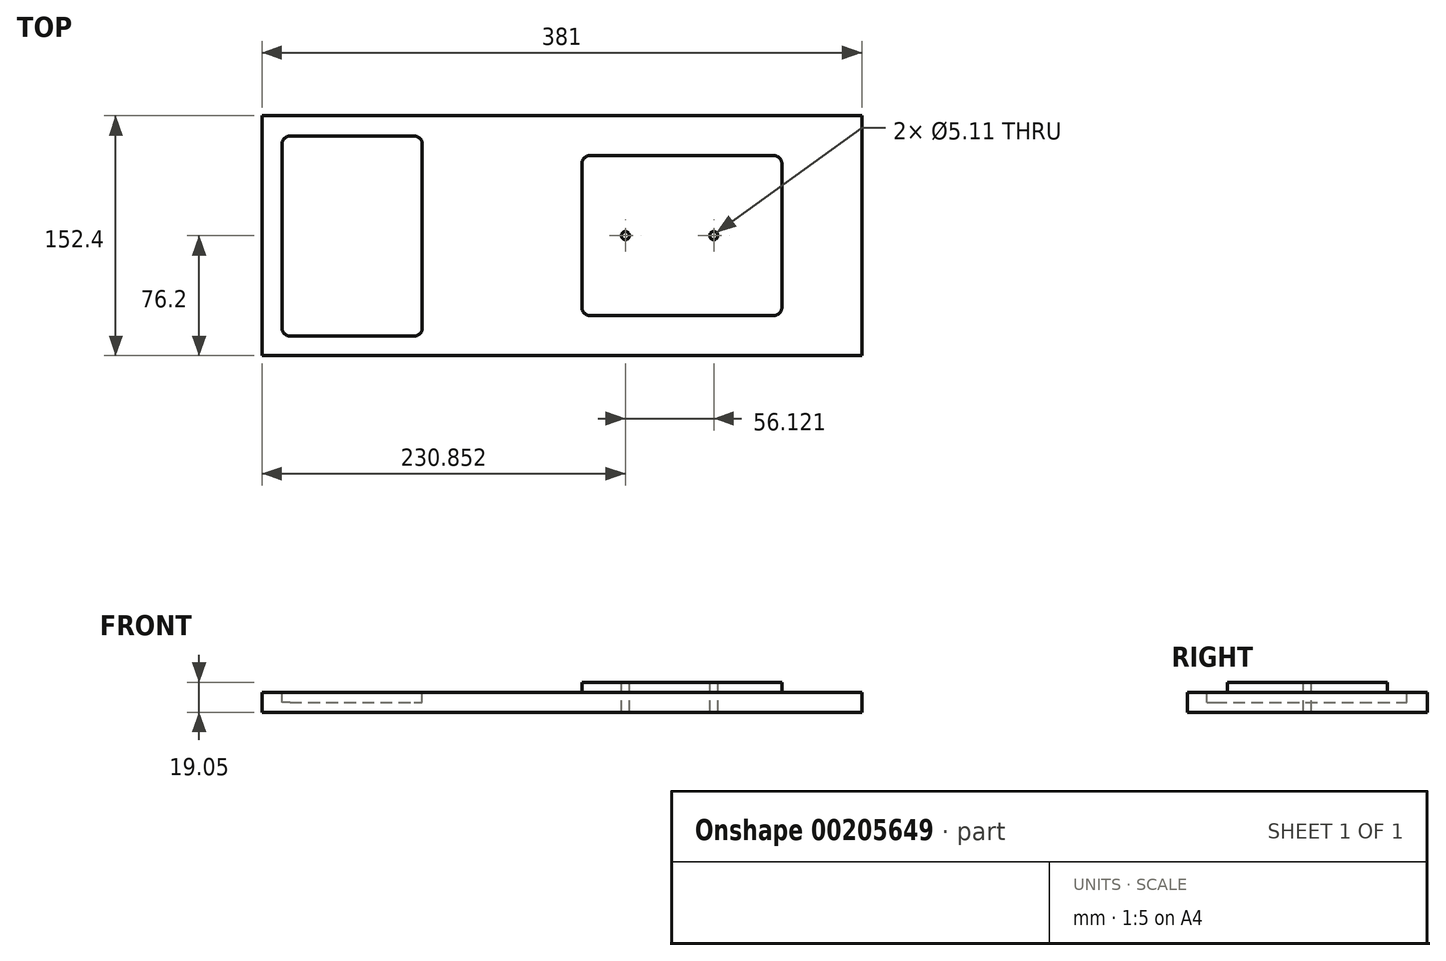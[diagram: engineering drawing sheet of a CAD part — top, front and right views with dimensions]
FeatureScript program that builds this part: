
annotation { "Feature Type Name" : "Feature", "Feature Type Description" : "" }
export const myFeature = defineFeature(function(context is Context, id is Id, definition is map)
    precondition{}
    {
        {
            var Q0;
            Q0=qCreatedBy(makeId("Top.planeOp"),FACE);
            var sketch = newSketch(context, id + "F0", { "sketchPlane" : qUnion([Q0])});
            skLineSegment(sketch, "E0.bottom", {"start": v(190.5, 76.2) * mm, "end": v(-190.5, 76.2) * mm});
            skLineSegment(sketch, "E0.top", {"start": v(190.5, -76.2) * mm, "end": v(-190.5, -76.2) * mm});
            skLineSegment(sketch, "E0.left", {"start": v(190.5, 76.2) * mm, "end": v(190.5, -76.2) * mm});
            skLineSegment(sketch, "E0.right", {"start": v(-190.5, 76.2) * mm, "end": v(-190.5, -76.2) * mm});
            skPoint(sketch, "E0.middle", {"position": v(0, 0) * mm});
            skSolve(sketch);
        }
        {
            var Q0;
            Q0=makeQuery(id+"F0.imprint","IMPRINT",FACE,{"disambiguationData":[TD([[makeQuery(id+"F0.imprint","IMPRINT",EDGE,{"derivedFrom":sQuery(id+"F0.wireOp",EDGE,"E0.bottom")}),1.0]])]});
            extrude(context, id + "F1", {"entities" : qUnion([Q0]), "depth" : 12.7 * mm});
        }
        {
            var Q0;
            Q0=makeQuery(id+"F1.opExtrude","CAP_FACE",FACE,{"disambiguationData":[OSD([sQuery(id+"F0.wireOp",EDGE,"E0.bottom"),sQuery(id+"F0.wireOp",EDGE,"E0.top"),sQuery(id+"F0.wireOp",EDGE,"E0.left"),sQuery(id+"F0.wireOp",EDGE,"E0.right")])],"isStart":false});
            var sketch = newSketch(context, id + "F2", { "sketchPlane" : qUnion([Q0])});
            skLineSegment(sketch, "E1.bottom", {"start": v(-177.8, -63.74) * mm, "end": v(-88.66, -63.74) * mm});
            skLineSegment(sketch, "E1.top", {"start": v(-177.8, 63.26) * mm, "end": v(-88.66, 63.26) * mm});
            skLineSegment(sketch, "E1.left", {"start": v(-177.8, -63.74) * mm, "end": v(-177.8, 63.26) * mm});
            skLineSegment(sketch, "E1.right", {"start": v(-88.66, -63.74) * mm, "end": v(-88.66, 63.26) * mm});
            skSolve(sketch);
        }
        {
            var Q0;
            Q0=makeQuery(id+"F2.imprint","IMPRINT",FACE,{"disambiguationData":[TD([[makeQuery(id+"F2.imprint","IMPRINT",EDGE,{"derivedFrom":sQuery(id+"F2.wireOp",EDGE,"E1.bottom")}),1.0]])]});
            extrude(context, id + "F3", {"entities" : qUnion([Q0]), "operationType" : NewBodyOperationType.REMOVE, "oppositeDirection" : true, "depth" : 6.35 * mm});
        }
        {
            var Q0;
            Q0=makeQuery(id+"F3.boolean.opBoolean","COPY",EDGE,{"derivedFrom":makeQuery(id+"F3.opExtrude","SWEPT_EDGE",EDGE,{"disambiguationData":[OSD([sQuery(id+"F2.wireOp",EDGE,"E1.top"),sQuery(id+"F2.wireOp",EDGE,"E1.left")])]})});
            var Q1;
            Q1=makeQuery(id+"F3.boolean.opBoolean","COPY",EDGE,{"derivedFrom":makeQuery(id+"F3.opExtrude","SWEPT_EDGE",EDGE,{"disambiguationData":[OSD([sQuery(id+"F2.wireOp",EDGE,"E1.bottom"),sQuery(id+"F2.wireOp",EDGE,"E1.left")])]})});
            var Q2;
            Q2=makeQuery(id+"F3.boolean.opBoolean","COPY",EDGE,{"derivedFrom":makeQuery(id+"F3.opExtrude","SWEPT_EDGE",EDGE,{"disambiguationData":[OSD([sQuery(id+"F2.wireOp",EDGE,"E1.top"),sQuery(id+"F2.wireOp",EDGE,"E1.right")])]})});
            var Q3;
            Q3=makeQuery(id+"F3.boolean.opBoolean","COPY",EDGE,{"derivedFrom":makeQuery(id+"F3.opExtrude","SWEPT_EDGE",EDGE,{"disambiguationData":[OSD([sQuery(id+"F2.wireOp",EDGE,"E1.bottom"),sQuery(id+"F2.wireOp",EDGE,"E1.right")])]})});
            fillet(context, id + "F4", {"entities" : qUnion([Q0, Q1, Q2, Q3]), "radius" : 5.08 * mm, "tangentPropagation" : true, "allowEdgeOverflow" : false});
        }
        {
            var Q0;
            Q0=makeQuery(id+"F1.opExtrude","CAP_FACE",FACE,{"disambiguationData":[OSD([sQuery(id+"F0.wireOp",EDGE,"E0.bottom"),sQuery(id+"F0.wireOp",EDGE,"E0.top"),sQuery(id+"F0.wireOp",EDGE,"E0.left"),sQuery(id+"F0.wireOp",EDGE,"E0.right")])],"isStart":false});
            var sketch = newSketch(context, id + "F5", { "sketchPlane" : qUnion([Q0])});
            skLineSegment(sketch, "E2", {"start": v(0, 0) * mm, "end": v(172.49, 0) * mm, "construction": true});
            skLineSegment(sketch, "E3.bottom", {"start": v(12.7, 50.8) * mm, "end": v(139.7, 50.8) * mm});
            skLineSegment(sketch, "E3.top", {"start": v(12.7, -50.8) * mm, "end": v(139.7, -50.8) * mm});
            skLineSegment(sketch, "E3.left", {"start": v(12.7, 50.8) * mm, "end": v(12.7, -50.8) * mm});
            skLineSegment(sketch, "E3.right", {"start": v(139.7, 50.8) * mm, "end": v(139.7, -50.8) * mm});
            skPoint(sketch, "E3.middle", {"position": v(76.2, 0) * mm});
            skSolve(sketch);
        }
        {
            var Q0;
            Q0=makeQuery(id+"F5.imprint","IMPRINT",FACE,{"disambiguationData":[TD([[makeQuery(id+"F5.imprint","IMPRINT",EDGE,{"derivedFrom":sQuery(id+"F5.wireOp",EDGE,"E3.bottom")}),-1.0]])]});
            extrude(context, id + "F6", {"entities" : qUnion([Q0]), "operationType" : NewBodyOperationType.ADD, "depth" : 6.35 * mm});
        }
        {
            var Q0;
            Q0=makeQuery(id+"F6.opExtrude","SWEPT_EDGE",EDGE,{"disambiguationData":[OSD([sQuery(id+"F5.wireOp",EDGE,"E3.top"),sQuery(id+"F5.wireOp",EDGE,"E3.left")])]});
            var Q1;
            Q1=makeQuery(id+"F6.opExtrude","SWEPT_EDGE",EDGE,{"disambiguationData":[OSD([sQuery(id+"F5.wireOp",EDGE,"E3.top"),sQuery(id+"F5.wireOp",EDGE,"E3.right")])]});
            var Q2;
            Q2=makeQuery(id+"F6.opExtrude","SWEPT_EDGE",EDGE,{"disambiguationData":[OSD([sQuery(id+"F5.wireOp",EDGE,"E3.bottom"),sQuery(id+"F5.wireOp",EDGE,"E3.right")])]});
            var Q3;
            Q3=makeQuery(id+"F6.opExtrude","SWEPT_EDGE",EDGE,{"disambiguationData":[OSD([sQuery(id+"F5.wireOp",EDGE,"E3.bottom"),sQuery(id+"F5.wireOp",EDGE,"E3.left")])]});
            fillet(context, id + "F7", {"entities" : qUnion([Q0, Q1, Q2, Q3]), "radius" : 5.08 * mm, "tangentPropagation" : true, "allowEdgeOverflow" : false});
        }
        {
            var Q0;
            Q0=makeQuery(id+"F6.opExtrude","CAP_FACE",FACE,{"disambiguationData":[OSD([sQuery(id+"F5.wireOp",EDGE,"E3.bottom"),sQuery(id+"F5.wireOp",EDGE,"E3.top"),sQuery(id+"F5.wireOp",EDGE,"E3.left"),sQuery(id+"F5.wireOp",EDGE,"E3.right")])],"isStart":false});
            var sketch = newSketch(context, id + "F8", { "sketchPlane" : qUnion([Q0])});
            skPoint(sketch, "E4", {"position": v(40.35, 0) * mm});
            skPoint(sketch, "E5", {"position": v(96.47, 0) * mm});
            skSolve(sketch);
        }
        {
            var Q0;
            Q0=sQuery(id+"F8.wireOp",VERTEX,"E4");
            var Q1;
            Q1=sQuery(id+"F8.wireOp",VERTEX,"E5");
            var Q2;
            Q2=makeQuery(id+"F1.opExtrude","SWEPT_BODY",BODY,{"disambiguationData":[OSD([sQuery(id+"F0.wireOp",EDGE,"E0.bottom"),sQuery(id+"F0.wireOp",EDGE,"E0.top"),sQuery(id+"F0.wireOp",EDGE,"E0.left"),sQuery(id+"F0.wireOp",EDGE,"E0.right")])]});
            hole(context, id + "F9", {"style" : HoleStyle.SIMPLE, "endStyle" : HoleEndStyle.THROUGH, "standardTappedOrClearance" : lookupTablePath({ "standard" : "ANSI", "engagement" : "75%", "pitch" : "20 tpi", "size" : "1/4", "type" : "Tapped" }), "standardBlindInLast" : lookupTablePath({ "standard" : "ANSI", "engagement" : "75%", "pitch" : "20 tpi", "size" : "1/4", "type" : "Tapped" }), "holeDiameter" : 5.1 * mm, "locations" : qUnion([Q0, Q1]), "scope" : qUnion([Q2]), "isTappedThrough" : true, "majorDiameter" : 6.35 * mm, "showTappedDepth" : true});
        }
    });
